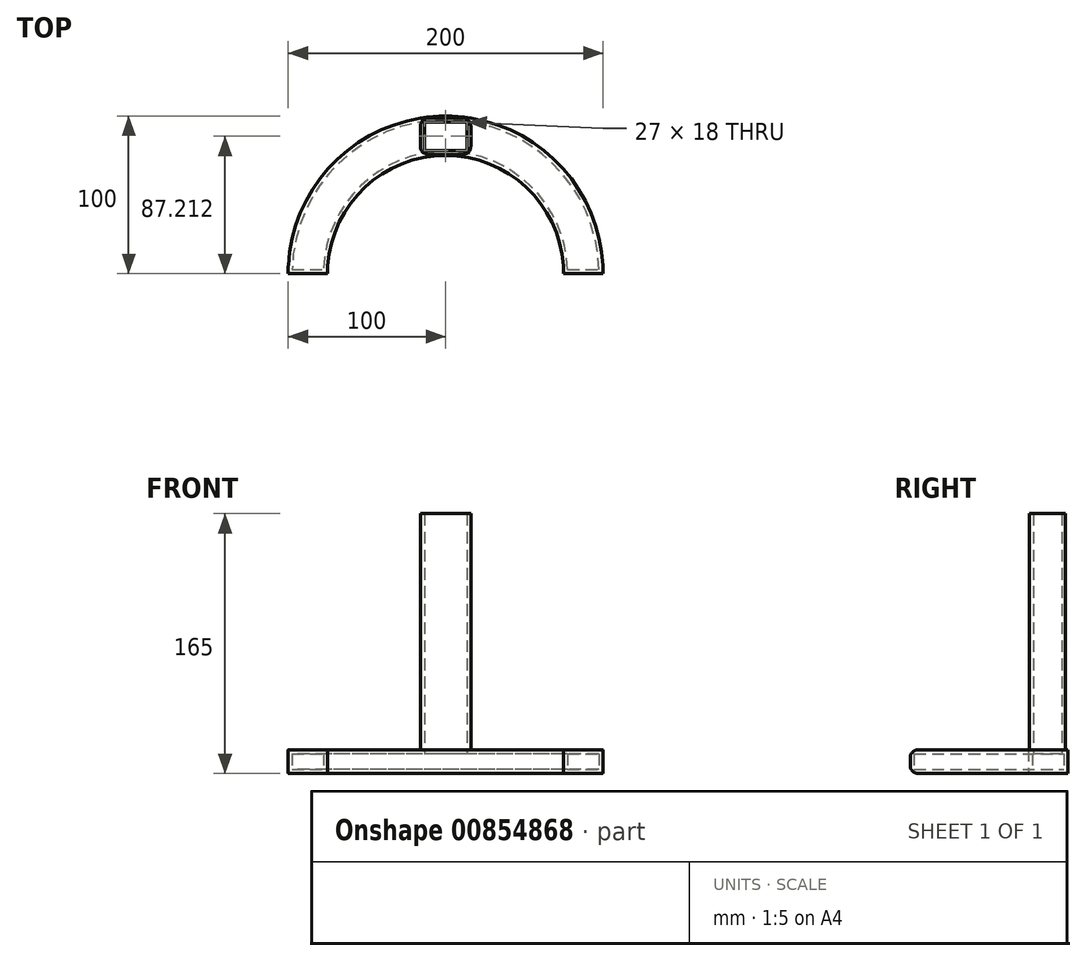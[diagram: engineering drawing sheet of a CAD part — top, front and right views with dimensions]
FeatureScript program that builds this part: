
annotation { "Feature Type Name" : "Feature", "Feature Type Description" : "" }
export const myFeature = defineFeature(function(context is Context, id is Id, definition is map)
    precondition{}
    {
        {
            var Q0;
            Q0=qCreatedBy(makeId("Top.planeOp"),FACE);
            var sketch = newSketch(context, id + "F0", { "sketchPlane" : qUnion([Q0])});
            skArc(sketch, "E0", {"start": v(100, 0) * mm, "mid": v(0, 100) * mm, "end": v(-100, 0) * mm});
            skLineSegment(sketch, "E1", {"start": v(-100, 0) * mm, "end": v(-75, 0) * mm});
            skArc(sketch, "E2", {"start": v(75, 0) * mm, "mid": v(0, 75) * mm, "end": v(-75, 0) * mm});
            skLineSegment(sketch, "E3.trimOffspring", {"start": v(75, 0) * mm, "end": v(100, 0) * mm});
            skSolve(sketch);
        }
        {
            var Q0;
            Q0=makeQuery(id+"F0.imprint","IMPRINT",FACE,{"disambiguationData":[TD([[makeQuery(id+"F0.imprint","IMPRINT",EDGE,{"derivedFrom":sQuery(id+"F0.wireOp",EDGE,"E0")}),1.0]])]});
            extrude(context, id + "F1", {"entities" : qUnion([Q0]), "depth" : 15 * mm, "offsetDistance" : 25 * mm});
        }
        {
            var Q0;
            Q0=makeQuery(id+"F1.opExtrude","CAP_FACE",FACE,{"disambiguationData":[OSD([sQuery(id+"F0.wireOp",EDGE,"E0"),sQuery(id+"F0.wireOp",EDGE,"E1"),sQuery(id+"F0.wireOp",EDGE,"E2"),sQuery(id+"F0.wireOp",EDGE,"E3.trimOffspring")])],"isStart":false});
            var sketch = newSketch(context, id + "F2", { "sketchPlane" : qUnion([Q0])});
            skLineSegment(sketch, "E4.bottom", {"start": v(16, 98.71) * mm, "end": v(-16, 98.71) * mm});
            skLineSegment(sketch, "E4.top", {"start": v(16, 75.71) * mm, "end": v(-16, 75.71) * mm});
            skLineSegment(sketch, "E4.left", {"start": v(16, 98.71) * mm, "end": v(16, 75.71) * mm});
            skLineSegment(sketch, "E4.right", {"start": v(-16, 98.71) * mm, "end": v(-16, 75.71) * mm});
            skPoint(sketch, "E4.middle", {"position": v(0, 87.21) * mm});
            skPoint(sketch, "E4.middle.positionSnap0", {"position": v(0, 75) * mm});
            skPoint(sketch, "E4.centerSnap0", {"position": v(0, 75) * mm});
            skSolve(sketch);
        }
        {
            var Q0;
            Q0=makeQuery(id+"F2.imprint","IMPRINT",FACE,{"disambiguationData":[TD([[makeQuery(id+"F2.imprint","IMPRINT",EDGE,{"derivedFrom":sQuery(id+"F2.wireOp",EDGE,"E4.bottom")}),1.0]])]});
            extrude(context, id + "F3", {"entities" : qUnion([Q0]), "operationType" : NewBodyOperationType.ADD, "depth" : 150 * mm, "offsetDistance" : 25 * mm});
        }
        {
            var Q0;
            Q0=makeQuery(id+"F3.opExtrude","CAP_FACE",FACE,{"disambiguationData":[OSD([sQuery(id+"F2.wireOp",EDGE,"E4.bottom"),sQuery(id+"F2.wireOp",EDGE,"E4.top"),sQuery(id+"F2.wireOp",EDGE,"E4.left"),sQuery(id+"F2.wireOp",EDGE,"E4.right")])],"isStart":false});
            shell(context, id + "F4", {"entities" : qUnion([Q0]), "thickness" : 2.5 * mm});
        }
        {
            var Q0;
            Q0=makeQuery(id+"F3.opExtrude","SWEPT_EDGE",EDGE,{"disambiguationData":[OSD([sQuery(id+"F2.wireOp",EDGE,"E4.top"),sQuery(id+"F2.wireOp",EDGE,"E4.right")])]});
            var Q1;
            Q1=makeQuery(id+"F3.opExtrude","SWEPT_EDGE",EDGE,{"disambiguationData":[OSD([sQuery(id+"F0.wireOp",EDGE,"E0"),sQuery(id+"F2.wireOp",EDGE,"E4.bottom"),sQuery(id+"F2.wireOp",EDGE,"E4.right")])]});
            var Q2;
            Q2=makeQuery(id+"F3.opExtrude","SWEPT_EDGE",EDGE,{"disambiguationData":[OSD([sQuery(id+"F0.wireOp",EDGE,"E0"),sQuery(id+"F2.wireOp",EDGE,"E4.bottom"),sQuery(id+"F2.wireOp",EDGE,"E4.left")])]});
            var Q3;
            Q3=makeQuery(id+"F3.opExtrude","SWEPT_EDGE",EDGE,{"disambiguationData":[OSD([sQuery(id+"F2.wireOp",EDGE,"E4.top"),sQuery(id+"F2.wireOp",EDGE,"E4.left")])]});
            var Q4;
            Q4=makeQuery(id+"F1.opExtrude","CAP_EDGE",EDGE,{"disambiguationData":[OSD([sQuery(id+"F0.wireOp",EDGE,"E1")])],"isStart":false});
            var Q5;
            Q5=makeQuery(id+"F1.opExtrude","CAP_EDGE",EDGE,{"disambiguationData":[OSD([sQuery(id+"F0.wireOp",EDGE,"E1")])],"isStart":true});
            var Q6;
            Q6=makeQuery(id+"F1.opExtrude","CAP_EDGE",EDGE,{"disambiguationData":[OSD([sQuery(id+"F0.wireOp",EDGE,"E3.trimOffspring")])],"isStart":false});
            var Q7;
            Q7=makeQuery(id+"F1.opExtrude","CAP_EDGE",EDGE,{"disambiguationData":[OSD([sQuery(id+"F0.wireOp",EDGE,"E3.trimOffspring")])],"isStart":true});
            fillet(context, id + "F5", {"entities" : qUnion([Q0, Q1, Q2, Q3, Q4, Q5, Q6, Q7]), "radius" : 5 * mm, "tangentPropagation" : true, "allowEdgeOverflow" : false});
        }
    });
